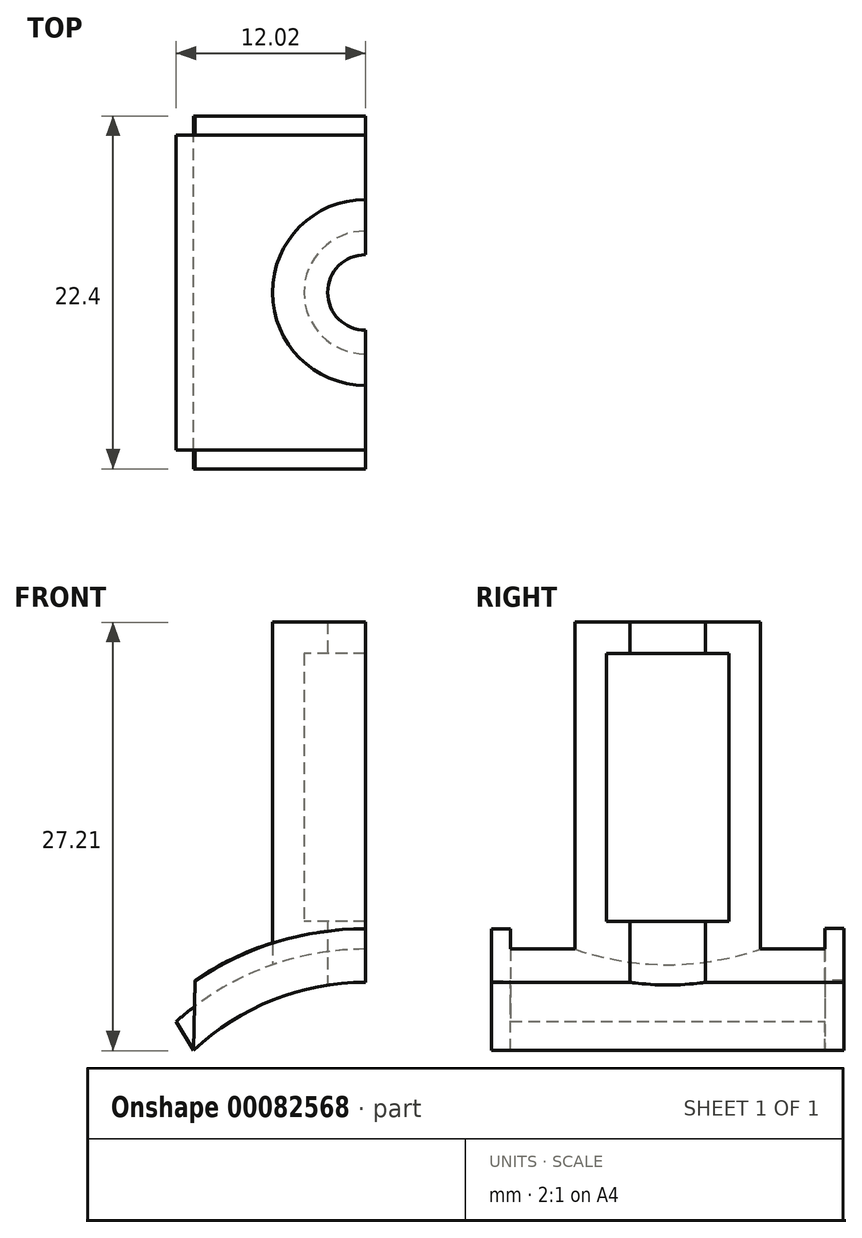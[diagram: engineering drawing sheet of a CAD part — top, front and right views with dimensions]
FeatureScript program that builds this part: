
annotation { "Feature Type Name" : "Feature", "Feature Type Description" : "" }
export const myFeature = defineFeature(function(context is Context, id is Id, definition is map)
    precondition{}
    {
        {
            var Q0;
            Q0=qCreatedBy(makeId("Front.planeOp"),FACE);
            var sketch = newSketch(context, id + "F0", { "sketchPlane" : qUnion([Q0])});
            skCircle(sketch, "E0", {"center": v(0, 0) * mm, "radius": 15.9 * mm, "construction": true});
            skLineSegment(sketch, "E1", {"start": v(-2.4, 15.72) * mm, "end": v(-2.4, 19.76) * mm});
            skLineSegment(sketch, "E2", {"start": v(-2.4, 19.76) * mm, "end": v(-3.9, 19.76) * mm});
            skLineSegment(sketch, "E3", {"start": v(-3.9, 19.76) * mm, "end": v(-3.9, 36.76) * mm});
            skLineSegment(sketch, "E4", {"start": v(-3.9, 36.76) * mm, "end": v(-2.4, 36.76) * mm});
            skLineSegment(sketch, "E5", {"start": v(-2.4, 36.76) * mm, "end": v(-2.4, 38.76) * mm});
            skLineSegment(sketch, "E6", {"start": v(-2.4, 38.76) * mm, "end": v(-5.9, 38.76) * mm});
            skLineSegment(sketch, "E7", {"start": v(-5.9, 38.76) * mm, "end": v(-5.9, 14.76) * mm});
            skLineSegment(sketch, "E8", {"start": v(-5.9, 14.76) * mm, "end": v(-2.4, 15.72) * mm});
            skLineSegment(sketch, "E9", {"start": v(0, 0) * mm, "end": v(0, 52.47) * mm, "construction": true});
            skSolve(sketch);
        }
        {
            var Q0;
            Q0=makeQuery(id+"F0.imprint","IMPRINT",FACE,{"disambiguationData":[TD([[makeQuery(id+"F0.imprint","IMPRINT",EDGE,{"derivedFrom":sQuery(id+"F0.wireOp",EDGE,"E1")}),1.0]])]});
            var Q1;
            Q1=sQuery(id+"F0.wireOp",EDGE,"E9");
            revolve(context, id + "F1", {"entities" : qUnion([Q0]), "axis" : qUnion([Q1]), "revolveType" : RevolveType.SYMMETRIC, "angle" : 180 * degree});
        }
        {
            var Q0;
            Q0=qCreatedBy(makeId("Front.planeOp"),FACE);
            var sketch = newSketch(context, id + "F2", { "sketchPlane" : qUnion([Q0])});
            skArc(sketch, "E10", {"start": v(0, 15.9) * mm, "mid": v(-5.88, 14.77) * mm, "end": v(-10.92, 11.55) * mm});
            skArc(sketch, "E11", {"start": v(0, 18) * mm, "mid": v(-6.43, 16.81) * mm, "end": v(-12.02, 13.4) * mm});
            skLineSegment(sketch, "E12", {"start": v(-10.92, 11.55) * mm, "end": v(-12.02, 13.4) * mm});
            skLineSegment(sketch, "E13", {"start": v(0, 15.9) * mm, "end": v(0, 18) * mm});
            skSolve(sketch);
        }
        {
            var Q0;
            Q0 = qSketchRegion(id + "F2", true);
            extrude(context, id + "F3", {"entities" : qUnion([Q0]), "operationType" : NewBodyOperationType.ADD, "endBound" : BoundingType.SYMMETRIC, "depth" : 20 * mm});
        }
        {
            var Q0;
            Q0=qCreatedBy(makeId("Front.planeOp"),FACE);
            var sketch = newSketch(context, id + "F4", { "sketchPlane" : qUnion([Q0])});
            skCircle(sketch, "E14", {"center": v(0, 0) * mm, "radius": 15.9 * mm});
            skSolve(sketch);
        }
        {
            var Q0;
            Q0 = qSketchRegion(id + "F4", true);
            extrude(context, id + "F5", {"entities" : qUnion([Q0]), "operationType" : NewBodyOperationType.REMOVE, "endBound" : BoundingType.SYMMETRIC, "oppositeDirection" : true, "depth" : 25 * mm});
        }
        {
            var Q0;
            Q0=makeQuery(id+"F1.opRevolve","SWEPT_FACE",FACE,{"disambiguationData":[OSD([sQuery(id+"F0.wireOp",EDGE,"E2")])]});
            var sketch = newSketch(context, id + "F6", { "sketchPlane" : qUnion([Q0])});
            skCircle(sketch, "E15", {"center": v(0, 0) * mm, "radius": 2.4 * mm});
            skSolve(sketch);
        }
        {
            var Q0;
            Q0 = qSketchRegion(id + "F6", true);
            extrude(context, id + "F7", {"entities" : qUnion([Q0]), "operationType" : NewBodyOperationType.REMOVE, "endBound" : BoundingType.THROUGH_ALL, "oppositeDirection" : true, "depth" : 25 * mm});
        }
        {
            var Q0;
            Q0=makeQuery(id+"F3.opExtrude","CAP_FACE",FACE,{"disambiguationData":[OSD([sQuery(id+"F2.wireOp",EDGE,"E10"),sQuery(id+"F2.wireOp",EDGE,"E11"),sQuery(id+"F2.wireOp",EDGE,"E12"),sQuery(id+"F2.wireOp",EDGE,"E13")])],"isStart":false});
            var sketch = newSketch(context, id + "F8", { "sketchPlane" : qUnion([Q0])});
            skArc(sketch, "E16", {"start": v(0, 15.9) * mm, "mid": v(-5.88, 14.77) * mm, "end": v(-10.92, 11.55) * mm});
            skArc(sketch, "E17", {"start": v(0, 19.3) * mm, "mid": v(-5.66, 18.44) * mm, "end": v(-10.81, 15.97) * mm});
            skLineSegment(sketch, "E18", {"start": v(-10.92, 11.55) * mm, "end": v(-10.81, 15.97) * mm});
            skLineSegment(sketch, "E19", {"start": v(0, 19.3) * mm, "end": v(0, 15.9) * mm});
            skSolve(sketch);
        }
        {
            var Q0;
            Q0 = qSketchRegion(id + "F8", true);
            extrude(context, id + "F9", {"entities" : qUnion([Q0]), "operationType" : NewBodyOperationType.ADD, "depth" : 1.2 * mm});
        }
        {
            var Q0;
            Q0=makeQuery(id+"F3.opExtrude","CAP_FACE",FACE,{"disambiguationData":[OSD([sQuery(id+"F2.wireOp",EDGE,"E10"),sQuery(id+"F2.wireOp",EDGE,"E11"),sQuery(id+"F2.wireOp",EDGE,"E12"),sQuery(id+"F2.wireOp",EDGE,"E13")])],"isStart":true});
            var sketch = newSketch(context, id + "F10", { "sketchPlane" : qUnion([Q0])});
            skArc(sketch, "E20", {"start": v(0, 15.9) * mm, "mid": v(5.88, 14.77) * mm, "end": v(10.92, 11.55) * mm});
            skArc(sketch, "E21", {"start": v(10.81, 16.02) * mm, "mid": v(5.65, 18.49) * mm, "end": v(0, 19.33) * mm});
            skLineSegment(sketch, "E22", {"start": v(0, 19.33) * mm, "end": v(0, 15.9) * mm});
            skLineSegment(sketch, "E23", {"start": v(10.81, 16.02) * mm, "end": v(10.92, 11.55) * mm});
            skSolve(sketch);
        }
        {
            var Q0;
            Q0 = qSketchRegion(id + "F10", true);
            extrude(context, id + "F11", {"entities" : qUnion([Q0]), "operationType" : NewBodyOperationType.ADD, "depth" : 1.2 * mm});
        }
    });
